# Revit family: UB90.xxx.S
name_source: partatom
category: Möbelsysteme
revit_build: Autodesk Revit 2015 (Build: 20140606_1530(x64)
units: mm (PartAtom-declared; Revit-internal decimal feet)

## types (20) — shared parameters
1400/600 2S 2nd lvl = Nein
Beschreibung = GS-tested safety storage underbench cabinets for unrestricted storage of flammable hazardous materials in work areas in accordance with EN 14470-1 and TRGS 510 with a fire resistance of 90 (Type 90)
Cabinet & door colour = RAL 7035 Light grey
Cabinet height = 600 mm
Diff. pressure (Air change 10 times) = 1.0 Pa
Double door 1400 = Nein
Hersteller = asecos GmbH
Price information = Price from fall 2017
Price information 2 = Prices are ex works and without taxes and shipping
Product video = https://www.youtube.com
Typenbild = <Keine Auswahl>
URL = https://www.asecos.com
ex. air pos. 2 = 130 mm  [stored 0.426509 ft]
zero-valued in all types: Drawer Pos. 1, Drawer Pos. 2

## per-type parameters (varying)
- UB90.060.089.S: 1100/500 2S 2nd lvl=Nein; 1100/500 2S perf. insert=Nein; 1100/500 2nd lvl=Nein; 1100/500 S perf. insert=Nein; 1100/600 2S 2nd lvl=Nein; 1100/600 2S perf. insert=Nein; 1100/600 2nd lvl=Nein; 1100/600 S perf. insert=Nein; 1400/500 2S 2nd lvl=Nein; 1400/500 2S perf. insert=Nein; 1400/600 2S perf. insert=Nein; 590/500 2nd lvl=Nein; 590/500 perf. insert=Nein; 590/600 2nd lvl=Nein; 590/600 perf. insert=Nein; 890/500 2nd lvl=Nein; 890/500 perf. insert=Nein; 890/600 2nd lvl=Nein; 890/600 perf. insert=Ja; Air change 10 times=0.6 L/s; Bestellnummer DACH=30457-001-30459; Cabinet depth=574 mm  [stored 1.8832 ft]; Cabinet width=893 mm  [stored 2.92979 ft]; Distributed load=3.07 kN/m²; Door width=839 mm; Door width RS=495 mm; Double door=Nein; Drawer depth=503 mm  [stored 1.65026 ft]; Drawer width 1=725 mm  [stored 2.37861 ft]; Drawer width 2=100 mm  [stored 0.328084 ft]; Handle LI=Nein; Handle LI pos=178 mm; Handle MI=Ja; Handle MI position=355 mm; Handle RE=Nein; Handle RE Pos=183 mm; Kosten=1693.5 $; Modell=UB90.060.089.S, light grey, drawer with perforated insert; Order No. Global=30457-001-30459; Single door=Ja; Sticker HI=Ja; Sticker LO=Nein; ex. air pos. 1=301 mm  [stored 0.987533 ft]
- UB90.060.059.050.S: 1100/500 2S 2nd lvl=Nein; 1100/500 2S perf. insert=Nein; 1100/500 2nd lvl=Nein; 1100/500 S perf. insert=Nein; 1100/600 2S 2nd lvl=Nein; 1100/600 2S perf. insert=Nein; 1100/600 2nd lvl=Nein; 1100/600 S perf. insert=Nein; 1400/500 2S 2nd lvl=Nein; 1400/500 2S perf. insert=Nein; 1400/600 2S perf. insert=Nein; 590/500 2nd lvl=Nein; 590/500 perf. insert=Ja; 590/600 2nd lvl=Nein; 590/600 perf. insert=Nein; 890/500 2nd lvl=Nein; 890/500 perf. insert=Nein; 890/600 2nd lvl=Nein; 890/600 perf. insert=Nein; Air change 10 times=0.3 L/s; Bestellnummer DACH=30473-001-35294 + 18922; Cabinet depth=503 mm  [stored 1.65026 ft]; Cabinet width=593 mm  [stored 1.94554 ft]; Distributed load=4.51 kN/m²; Door width=539 mm; Door width RS=495 mm; Double door=Nein; Drawer depth=431 mm  [stored 1.41404 ft]; Drawer width 1=425 mm  [stored 1.39436 ft]; Drawer width 2=100 mm  [stored 0.328084 ft]; Handle LI=Nein; Handle LI pos=178 mm; Handle MI=Ja; Handle MI position=205 mm; Handle RE=Nein; Handle RE Pos=183 mm; Kosten=1293 $; Modell=UB90.060.059.050.S, light grey, drawer with perforated insert; Order No. Global=30473-001-35294 + 18922; Single door=Ja; Sticker HI=Nein; Sticker LO=Ja; ex. air pos. 1=182 mm
- UB90.060.059.S: 1100/500 2S 2nd lvl=Nein; 1100/500 2S perf. insert=Nein; 1100/500 2nd lvl=Nein; 1100/500 S perf. insert=Nein; 1100/600 2S 2nd lvl=Nein; 1100/600 2S perf. insert=Nein; 1100/600 2nd lvl=Nein; 1100/600 S perf. insert=Nein; 1400/500 2S 2nd lvl=Nein; 1400/500 2S perf. insert=Nein; 1400/600 2S perf. insert=Nein; 590/500 2nd lvl=Nein; 590/500 perf. insert=Nein; 590/600 2nd lvl=Nein; 590/600 perf. insert=Ja; 890/500 2nd lvl=Nein; 890/500 perf. insert=Nein; 890/600 2nd lvl=Nein; 890/600 perf. insert=Nein; Air change 10 times=0.3 L/s; Bestellnummer DACH=30472-001-30474; Cabinet depth=574 mm  [stored 1.8832 ft]; Cabinet width=593 mm  [stored 1.94554 ft]; Distributed load=4.41 kN/m²; Door width=539 mm; Door width RS=495 mm; Double door=Nein; Drawer depth=503 mm  [stored 1.65026 ft]; Drawer width 1=425 mm  [stored 1.39436 ft]; Drawer width 2=100 mm  [stored 0.328084 ft]; Handle LI=Nein; Handle LI pos=178 mm; Handle MI=Ja; Handle MI position=205 mm; Handle RE=Nein; Handle RE Pos=183 mm; Kosten=1336.5 $; Modell=UB90.060.059.S, light grey, drawer with perforated insert; Order No. Global=30472-001-30474; Single door=Ja; Sticker HI=Nein; Sticker LO=Ja; ex. air pos. 1=182 mm
- UB90.060.110.050.2S: 1100/500 2S 2nd lvl=Nein; 1100/500 2S perf. insert=Ja; 1100/500 2nd lvl=Nein; 1100/500 S perf. insert=Nein; 1100/600 2S 2nd lvl=Nein; 1100/600 2S perf. insert=Nein; 1100/600 2nd lvl=Nein; 1100/600 S perf. insert=Nein; 1400/500 2S 2nd lvl=Nein; 1400/500 2S perf. insert=Nein; 1400/600 2S perf. insert=Nein; 590/500 2nd lvl=Nein; 590/500 perf. insert=Nein; 590/600 2nd lvl=Nein; 590/600 perf. insert=Nein; 890/500 2nd lvl=Nein; 890/500 perf. insert=Nein; 890/600 2nd lvl=Nein; 890/600 perf. insert=Nein; Air change 10 times=0.6 L/s; Bestellnummer DACH=30428-001-35336; Cabinet depth=503 mm  [stored 1.65026 ft]; Cabinet width=1102 mm  [stored 3.61549 ft]; Distributed load=2.73 kN/m²; Door width=521 mm  [stored 1.70932 ft]; Door width RS=521 mm  [stored 1.70932 ft]; Double door=Ja; Drawer depth=431 mm  [stored 1.41404 ft]; Drawer width 1=425 mm  [stored 1.39436 ft]; Drawer width 2=425 mm  [stored 1.39436 ft]; Handle LI=Ja; Handle LI pos=178 mm; Handle MI=Nein; Handle MI position=197 mm; Handle RE=Ja; Handle RE Pos=197 mm; Kosten=2177 $; Modell=UB90.060.110.050.2S, light grey, drawer with perforated insert; Order No. Global=30428-001-35336; Single door=Nein; Sticker HI=Ja; Sticker LO=Nein; ex. air pos. 1=301 mm  [stored 0.987533 ft]
- UB90.060.089.050.S: 1100/500 2S 2nd lvl=Nein; 1100/500 2S perf. insert=Nein; 1100/500 2nd lvl=Nein; 1100/500 S perf. insert=Nein; 1100/600 2S 2nd lvl=Nein; 1100/600 2S perf. insert=Nein; 1100/600 2nd lvl=Nein; 1100/600 S perf. insert=Nein; 1400/500 2S 2nd lvl=Nein; 1400/500 2S perf. insert=Nein; 1400/600 2S perf. insert=Nein; 590/500 2nd lvl=Nein; 590/500 perf. insert=Nein; 590/600 2nd lvl=Nein; 590/600 perf. insert=Nein; 890/500 2nd lvl=Nein; 890/500 perf. insert=Ja; 890/600 2nd lvl=Nein; 890/600 perf. insert=Nein; Air change 10 times=0.3 L/s; Bestellnummer DACH=30458-001-35307; Cabinet depth=503 mm  [stored 1.65026 ft]; Cabinet width=893 mm  [stored 2.92979 ft]; Distributed load=3.11 kN/m²; Door width=839 mm; Door width RS=495 mm; Double door=Nein; Drawer depth=431 mm  [stored 1.41404 ft]; Drawer width 1=725 mm  [stored 2.37861 ft]; Drawer width 2=100 mm  [stored 0.328084 ft]; Handle LI=Nein; Handle LI pos=178 mm; Handle MI=Ja; Handle MI position=355 mm; Handle RE=Nein; Handle RE Pos=183 mm; Kosten=1630 $; Modell=UB90.060.089.050.S, light grey, drawer with perforated insert; Order No. Global=30458-001-35307; Single door=Ja; Sticker HI=Ja; Sticker LO=Nein; ex. air pos. 1=301 mm  [stored 0.987533 ft]
- UB90.060.110.2S: 1100/500 2S 2nd lvl=Nein; 1100/500 2S perf. insert=Nein; 1100/500 2nd lvl=Nein; 1100/500 S perf. insert=Nein; 1100/600 2S 2nd lvl=Nein; 1100/600 2S perf. insert=Ja; 1100/600 2nd lvl=Nein; 1100/600 S perf. insert=Nein; 1400/500 2S 2nd lvl=Nein; 1400/500 2S perf. insert=Nein; 1400/600 2S perf. insert=Nein; 590/500 2nd lvl=Nein; 590/500 perf. insert=Nein; 590/600 2nd lvl=Nein; 590/600 perf. insert=Nein; 890/500 2nd lvl=Nein; 890/500 perf. insert=Nein; 890/600 2nd lvl=Nein; 890/600 perf. insert=Nein; Air change 10 times=0.6 L/s; Bestellnummer DACH=30427-001-30430; Cabinet depth=574 mm  [stored 1.8832 ft]; Cabinet width=1102 mm  [stored 3.61549 ft]; Distributed load=2.72 kN/m²; Door width=521 mm  [stored 1.70932 ft]; Door width RS=521 mm  [stored 1.70932 ft]; Double door=Ja; Drawer depth=503 mm  [stored 1.65026 ft]; Drawer width 1=425 mm  [stored 1.39436 ft]; Drawer width 2=425 mm  [stored 1.39436 ft]; Handle LI=Ja; Handle LI pos=175 mm  [stored 0.574147 ft]; Handle MI=Nein; Handle MI position=197 mm; Handle RE=Ja; Handle RE Pos=47 mm  [stored 0.154199 ft]; Kosten=2264 $; Modell=UB90.060.110.2S, light grey, drawer with perforated insert; Order No. Global=30427-001-30430; Single door=Nein; Sticker HI=Ja; Sticker LO=Nein; ex. air pos. 1=301 mm  [stored 0.987533 ft]
- UB90.060.140.2S: 1100/500 2S 2nd lvl=Nein; 1100/500 2S perf. insert=Nein; 1100/500 2nd lvl=Nein; 1100/500 S perf. insert=Nein; 1100/600 2S 2nd lvl=Nein; 1100/600 2S perf. insert=Nein; 1100/600 2nd lvl=Nein; 1100/600 S perf. insert=Nein; 1400/500 2S 2nd lvl=Nein; 1400/500 2S perf. insert=Nein; 1400/600 2S perf. insert=Ja; 590/500 2nd lvl=Nein; 590/500 perf. insert=Nein; 590/600 2nd lvl=Nein; 590/600 perf. insert=Nein; 890/500 2nd lvl=Nein; 890/500 perf. insert=Nein; 890/600 2nd lvl=Nein; 890/600 perf. insert=Nein; Air change 10 times=0.8 L/s; Bestellnummer DACH=30401-001-30404; Cabinet depth=574 mm  [stored 1.8832 ft]; Cabinet width=1402 mm  [stored 4.59974 ft]; Distributed load=2.35 kN/m²; Door width=821 mm  [stored 2.69357 ft]; Door width RS=521 mm  [stored 1.70932 ft]; Double door=Ja; Drawer depth=503 mm  [stored 1.65026 ft]; Drawer width 1=725 mm  [stored 2.37861 ft]; Drawer width 2=425 mm  [stored 1.39436 ft]; Handle LI=Nein; Handle LI pos=175 mm  [stored 0.574147 ft]; Handle MI=Ja; Handle MI position=347 mm; Handle RE=Ja; Handle RE Pos=47 mm  [stored 0.154199 ft]; Kosten=2370 $; Modell=UB90.060.140.2S, light grey, drawer with perforated insert; Order No. Global=30401-001-30404; Single door=Nein; Sticker HI=Ja; Sticker LO=Nein; ex. air pos. 1=301 mm  [stored 0.987533 ft]
- UB90.060.110.S: 1100/500 2S 2nd lvl=Nein; 1100/500 2S perf. insert=Nein; 1100/500 2nd lvl=Nein; 1100/500 S perf. insert=Nein; 1100/600 2S 2nd lvl=Nein; 1100/600 2S perf. insert=Nein; 1100/600 2nd lvl=Nein; 1100/600 S perf. insert=Ja; 1400/500 2S 2nd lvl=Nein; 1400/500 2S perf. insert=Nein; 1400/600 2S perf. insert=Nein; 590/500 2nd lvl=Nein; 590/500 perf. insert=Nein; 590/600 2nd lvl=Nein; 590/600 perf. insert=Nein; 890/500 2nd lvl=Nein; 890/500 perf. insert=Nein; 890/600 2nd lvl=Nein; 890/600 perf. insert=Nein; Air change 10 times=0.6 L/s; Bestellnummer DACH=30420-001-30423; Cabinet depth=574 mm  [stored 1.8832 ft]; Cabinet width=1102 mm  [stored 3.61549 ft]; Distributed load=2.72 kN/m²; Door width=1048 mm; Door width RS=495 mm; Double door=Nein; Drawer depth=503 mm  [stored 1.65026 ft]; Drawer width 1=934 mm  [stored 3.0643 ft]; Drawer width 2=100 mm  [stored 0.328084 ft]; Handle LI=Nein; Handle LI pos=178 mm; Handle MI=Ja; Handle MI position=460 mm; Handle RE=Nein; Handle RE Pos=183 mm; Kosten=1761 $; Modell=UB90.060.110.S, light grey, drawer with perforated insert; Order No. Global=30420-001-30423; Single door=Ja; Sticker HI=Ja; Sticker LO=Nein; ex. air pos. 1=301 mm  [stored 0.987533 ft]
- UB90.060.110.050.S: 1100/500 2S 2nd lvl=Nein; 1100/500 2S perf. insert=Nein; 1100/500 2nd lvl=Nein; 1100/500 S perf. insert=Ja; 1100/600 2S 2nd lvl=Nein; 1100/600 2S perf. insert=Nein; 1100/600 2nd lvl=Nein; 1100/600 S perf. insert=Nein; 1400/500 2S 2nd lvl=Nein; 1400/500 2S perf. insert=Nein; 1400/600 2S perf. insert=Nein; 590/500 2nd lvl=Nein; 590/500 perf. insert=Nein; 590/600 2nd lvl=Nein; 590/600 perf. insert=Nein; 890/500 2nd lvl=Nein; 890/500 perf. insert=Nein; 890/600 2nd lvl=Nein; 890/600 perf. insert=Nein; Air change 10 times=0.6 L/s; Bestellnummer DACH=30421-001-35339; Cabinet depth=503 mm  [stored 1.65026 ft]; Cabinet width=1102 mm  [stored 3.61549 ft]; Distributed load=2.73 kN/m²; Door width=1048 mm; Door width RS=495 mm; Double door=Nein; Drawer depth=431 mm  [stored 1.41404 ft]; Drawer width 1=934 mm  [stored 3.0643 ft]; Drawer width 2=100 mm  [stored 0.328084 ft]; Handle LI=Nein; Handle LI pos=178 mm; Handle MI=Ja; Handle MI position=460 mm; Handle RE=Nein; Handle RE Pos=183 mm; Kosten=1682 $; Modell=UB90.060.110.050.S, light grey, drawer with perforated insert; Order No. Global=30421-001-35339; Single door=Ja; Sticker HI=Ja; Sticker LO=Nein; ex. air pos. 1=301 mm  [stored 0.987533 ft]
- UB90.060.140.050.2S: 1100/500 2S 2nd lvl=Nein; 1100/500 2S perf. insert=Nein; 1100/500 2nd lvl=Nein; 1100/500 S perf. insert=Nein; 1100/600 2S 2nd lvl=Nein; 1100/600 2S perf. insert=Nein; 1100/600 2nd lvl=Nein; 1100/600 S perf. insert=Nein; 1400/500 2S 2nd lvl=Nein; 1400/500 2S perf. insert=Ja; 1400/600 2S perf. insert=Nein; 590/500 2nd lvl=Nein; 590/500 perf. insert=Nein; 590/600 2nd lvl=Nein; 590/600 perf. insert=Nein; 890/500 2nd lvl=Nein; 890/500 perf. insert=Nein; 890/600 2nd lvl=Nein; 890/600 perf. insert=Nein; Air change 10 times=0.8 L/s; Bestellnummer DACH=30402-001-35358 + 18922; Cabinet depth=503 mm  [stored 1.65026 ft]; Cabinet width=1402 mm  [stored 4.59974 ft]; Distributed load=2.35 kN/m²; Door width=821 mm  [stored 2.69357 ft]; Door width RS=521 mm  [stored 1.70932 ft]; Double door=Ja; Drawer depth=431 mm  [stored 1.41404 ft]; Drawer width 1=725 mm  [stored 2.37861 ft]; Drawer width 2=425 mm  [stored 1.39436 ft]; Handle LI=Nein; Handle LI pos=175 mm  [stored 0.574147 ft]; Handle MI=Ja; Handle MI position=347 mm; Handle RE=Ja; Handle RE Pos=47 mm  [stored 0.154199 ft]; Kosten=2263 $; Modell=UB90.060.140.050.2S, light grey, drawer with perforated insert; Order No. Global=30402-001-35358 + 18922; Single door=Nein; Sticker HI=Ja; Sticker LO=Nein; ex. air pos. 1=301 mm  [stored 0.987533 ft]
- UB90.060.059.050.S with second level drawer: 1100/500 2S 2nd lvl=Nein; 1100/500 2S perf. insert=Nein; 1100/500 2nd lvl=Nein; 1100/500 S perf. insert=Nein; 1100/600 2S 2nd lvl=Nein; 1100/600 2S perf. insert=Nein; 1100/600 2nd lvl=Nein; 1100/600 S perf. insert=Nein; 1400/500 2S 2nd lvl=Nein; 1400/500 2S perf. insert=Nein; 1400/600 2S perf. insert=Nein; 590/500 2nd lvl=Ja; 590/500 perf. insert=Ja; 590/600 2nd lvl=Nein; 590/600 perf. insert=Nein; 890/500 2nd lvl=Nein; 890/500 perf. insert=Nein; 890/600 2nd lvl=Nein; 890/600 perf. insert=Nein; Air change 10 times=0.3 L/s; Bestellnummer DACH=30473-001-35294 + 18922 + 16595; Cabinet depth=503 mm  [stored 1.65026 ft]; Cabinet width=593 mm  [stored 1.94554 ft]; Distributed load=4.51 kN/m²; Door width=539 mm; Door width RS=495 mm; Double door=Nein; Drawer depth=431 mm  [stored 1.41404 ft]; Drawer width 1=425 mm  [stored 1.39436 ft]; Drawer width 2=100 mm  [stored 0.328084 ft]; Handle LI=Nein; Handle LI pos=178 mm; Handle MI=Ja; Handle MI position=205 mm; Handle RE=Nein; Handle RE Pos=183 mm; Kosten=1452 $; Modell=UB90.060.059.050.S, light grey, drawer with perforated insert, second level drawer; Order No. Global=30473-001-35294 + 18922 + 16595; Single door=Ja; Sticker HI=Nein; Sticker LO=Ja; ex. air pos. 1=182 mm
- UB90.060.059.S with second level drawer: 1100/500 2S 2nd lvl=Nein; 1100/500 2S perf. insert=Nein; 1100/500 2nd lvl=Nein; 1100/500 S perf. insert=Nein; 1100/600 2S 2nd lvl=Nein; 1100/600 2S perf. insert=Nein; 1100/600 2nd lvl=Nein; 1100/600 S perf. insert=Nein; 1400/500 2S 2nd lvl=Nein; 1400/500 2S perf. insert=Nein; 1400/600 2S perf. insert=Nein; 590/500 2nd lvl=Nein; 590/500 perf. insert=Nein; 590/600 2nd lvl=Ja; 590/600 perf. insert=Ja; 890/500 2nd lvl=Nein; 890/500 perf. insert=Nein; 890/600 2nd lvl=Nein; 890/600 perf. insert=Nein; Air change 10 times=0.3 L/s; Bestellnummer DACH=30472-001-30475; Cabinet depth=574 mm  [stored 1.8832 ft]; Cabinet width=593 mm  [stored 1.94554 ft]; Distributed load=4.41 kN/m²; Door width=539 mm; Door width RS=495 mm; Double door=Nein; Drawer depth=503 mm  [stored 1.65026 ft]; Drawer width 1=425 mm  [stored 1.39436 ft]; Drawer width 2=100 mm  [stored 0.328084 ft]; Handle LI=Nein; Handle LI pos=178 mm; Handle MI=Ja; Handle MI position=205 mm; Handle RE=Nein; Handle RE Pos=183 mm; Kosten=1465.5 $; Modell=UB90.060.059.S, light grey, drawer with perforated insert, second level drawer; Order No. Global=30472-001-30475; Single door=Ja; Sticker HI=Nein; Sticker LO=Ja; ex. air pos. 1=182 mm
- UB90.060.089.050.S with second level drawer: 1100/500 2S 2nd lvl=Nein; 1100/500 2S perf. insert=Nein; 1100/500 2nd lvl=Nein; 1100/500 S perf. insert=Nein; 1100/600 2S 2nd lvl=Nein; 1100/600 2S perf. insert=Nein; 1100/600 2nd lvl=Nein; 1100/600 S perf. insert=Nein; 1400/500 2S 2nd lvl=Nein; 1400/500 2S perf. insert=Nein; 1400/600 2S perf. insert=Nein; 590/500 2nd lvl=Nein; 590/500 perf. insert=Nein; 590/600 2nd lvl=Nein; 590/600 perf. insert=Nein; 890/500 2nd lvl=Ja; 890/500 perf. insert=Ja; 890/600 2nd lvl=Nein; 890/600 perf. insert=Nein; Air change 10 times=0.3 L/s; Bestellnummer DACH=30458-001-35307 + 16589; Cabinet depth=503 mm  [stored 1.65026 ft]; Cabinet width=893 mm  [stored 2.92979 ft]; Distributed load=3.11 kN/m²; Door width=839 mm; Door width RS=495 mm; Double door=Nein; Drawer depth=431 mm  [stored 1.41404 ft]; Drawer width 1=725 mm  [stored 2.37861 ft]; Drawer width 2=100 mm  [stored 0.328084 ft]; Handle LI=Nein; Handle LI pos=178 mm; Handle MI=Ja; Handle MI position=355 mm; Handle RE=Nein; Handle RE Pos=183 mm; Kosten=1803 $; Modell=UB90.060.089.050.S, light grey, drawer with perforated insert, second level drawer; Order No. Global=30458-001-35307 + 16589; Single door=Ja; Sticker HI=Ja; Sticker LO=Nein; ex. air pos. 1=301 mm  [stored 0.987533 ft]
- UB90.060.089.S with second level drawer: 1100/500 2S 2nd lvl=Nein; 1100/500 2S perf. insert=Nein; 1100/500 2nd lvl=Nein; 1100/500 S perf. insert=Nein; 1100/600 2S 2nd lvl=Nein; 1100/600 2S perf. insert=Nein; 1100/600 2nd lvl=Nein; 1100/600 S perf. insert=Nein; 1400/500 2S 2nd lvl=Nein; 1400/500 2S perf. insert=Nein; 1400/600 2S perf. insert=Nein; 590/500 2nd lvl=Nein; 590/500 perf. insert=Nein; 590/600 2nd lvl=Nein; 590/600 perf. insert=Nein; 890/500 2nd lvl=Nein; 890/500 perf. insert=Nein; 890/600 2nd lvl=Ja; 890/600 perf. insert=Ja; Air change 10 times=0.6 L/s; Bestellnummer DACH=30457-001-30460; Cabinet depth=574 mm  [stored 1.8832 ft]; Cabinet width=893 mm  [stored 2.92979 ft]; Distributed load=3.07 kN/m²; Door width=839 mm; Door width RS=495 mm; Double door=Nein; Drawer depth=503 mm  [stored 1.65026 ft]; Drawer width 1=725 mm  [stored 2.37861 ft]; Drawer width 2=100 mm  [stored 0.328084 ft]; Handle LI=Nein; Handle LI pos=178 mm; Handle MI=Ja; Handle MI position=355 mm; Handle RE=Nein; Handle RE Pos=183 mm; Kosten=1830.5 $; Modell=UB90.060.089.S, light grey, drawer with perforated insert, second level drawer; Order No. Global=30457-001-30460; Single door=Ja; Sticker HI=Ja; Sticker LO=Nein; ex. air pos. 1=301 mm  [stored 0.987533 ft]
- UB90.060.110.050.2S with second level drawer: 1100/500 2S 2nd lvl=Ja; 1100/500 2S perf. insert=Ja; 1100/500 2nd lvl=Nein; 1100/500 S perf. insert=Nein; 1100/600 2S 2nd lvl=Nein; 1100/600 2S perf. insert=Nein; 1100/600 2nd lvl=Nein; 1100/600 S perf. insert=Nein; 1400/500 2S 2nd lvl=Nein; 1400/500 2S perf. insert=Nein; 1400/600 2S perf. insert=Nein; 590/500 2nd lvl=Nein; 590/500 perf. insert=Nein; 590/600 2nd lvl=Nein; 590/600 perf. insert=Nein; 890/500 2nd lvl=Nein; 890/500 perf. insert=Nein; 890/600 2nd lvl=Nein; 890/600 perf. insert=Nein; Air change 10 times=0.6 L/s; Bestellnummer DACH=30428-001-35336 + 16590; Cabinet depth=503 mm  [stored 1.65026 ft]; Cabinet width=1102 mm  [stored 3.61549 ft]; Distributed load=2.73 kN/m²; Door width=521 mm  [stored 1.70932 ft]; Door width RS=521 mm  [stored 1.70932 ft]; Double door=Ja; Drawer depth=431 mm  [stored 1.41404 ft]; Drawer width 1=425 mm  [stored 1.39436 ft]; Drawer width 2=425 mm  [stored 1.39436 ft]; Handle LI=Ja; Handle LI pos=178 mm; Handle MI=Nein; Handle MI position=197 mm; Handle RE=Ja; Handle RE Pos=197 mm; Kosten=2347 $; Modell=UB90.060.110.050.2S, light grey, drawer with perforated insert,second level drawer; Order No. Global=30428-001-35336 + 16590; Single door=Nein; Sticker HI=Ja; Sticker LO=Nein; ex. air pos. 1=301 mm  [stored 0.987533 ft]
- UB90.060.110.050.S with second level drawer: 1100/500 2S 2nd lvl=Nein; 1100/500 2S perf. insert=Nein; 1100/500 2nd lvl=Ja; 1100/500 S perf. insert=Ja; 1100/600 2S 2nd lvl=Nein; 1100/600 2S perf. insert=Nein; 1100/600 2nd lvl=Nein; 1100/600 S perf. insert=Nein; 1400/500 2S 2nd lvl=Nein; 1400/500 2S perf. insert=Nein; 1400/600 2S perf. insert=Nein; 590/500 2nd lvl=Nein; 590/500 perf. insert=Nein; 590/600 2nd lvl=Nein; 590/600 perf. insert=Nein; 890/500 2nd lvl=Nein; 890/500 perf. insert=Nein; 890/600 2nd lvl=Nein; 890/600 perf. insert=Nein; Air change 10 times=0.6 L/s; Bestellnummer DACH=30421-001-35339 + 16592; Cabinet depth=503 mm  [stored 1.65026 ft]; Cabinet width=1102 mm  [stored 3.61549 ft]; Distributed load=2.73 kN/m²; Door width=1048 mm; Door width RS=495 mm; Double door=Nein; Drawer depth=431 mm  [stored 1.41404 ft]; Drawer width 1=934 mm  [stored 3.0643 ft]; Drawer width 2=100 mm  [stored 0.328084 ft]; Handle LI=Nein; Handle LI pos=178 mm; Handle MI=Ja; Handle MI position=460 mm; Handle RE=Nein; Handle RE Pos=183 mm; Kosten=1861 $; Modell=UB90.060.110.050.S, light grey, drawer with perforated insert, second level drawer; Order No. Global=30421-001-35339 + 16592; Single door=Ja; Sticker HI=Ja; Sticker LO=Nein; ex. air pos. 1=301 mm  [stored 0.987533 ft]
- UB90.060.110.2S with second level drawer: 1100/500 2S 2nd lvl=Nein; 1100/500 2S perf. insert=Nein; 1100/500 2nd lvl=Nein; 1100/500 S perf. insert=Nein; 1100/600 2S 2nd lvl=Ja; 1100/600 2S perf. insert=Ja; 1100/600 2nd lvl=Nein; 1100/600 S perf. insert=Nein; 1400/500 2S 2nd lvl=Nein; 1400/500 2S perf. insert=Nein; 1400/600 2S perf. insert=Nein; 590/500 2nd lvl=Nein; 590/500 perf. insert=Nein; 590/600 2nd lvl=Nein; 590/600 perf. insert=Nein; 890/500 2nd lvl=Nein; 890/500 perf. insert=Nein; 890/600 2nd lvl=Nein; 890/600 perf. insert=Nein; Air change 10 times=0.6 L/s; Bestellnummer DACH=30427-001-30431; Cabinet depth=574 mm  [stored 1.8832 ft]; Cabinet width=1102 mm  [stored 3.61549 ft]; Distributed load=2.72 kN/m²; Door width=521 mm  [stored 1.70932 ft]; Door width RS=521 mm  [stored 1.70932 ft]; Double door=Ja; Drawer depth=503 mm  [stored 1.65026 ft]; Drawer width 1=425 mm  [stored 1.39436 ft]; Drawer width 2=425 mm  [stored 1.39436 ft]; Handle LI=Ja; Handle LI pos=175 mm  [stored 0.574147 ft]; Handle MI=Nein; Handle MI position=197 mm; Handle RE=Ja; Handle RE Pos=47 mm  [stored 0.154199 ft]; Kosten=2522 $; Modell=UB90.060.110.2S, light grey, drawer with perforated insert, second level drawer; Order No. Global=30427-001-30431; Single door=Nein; Sticker HI=Ja; Sticker LO=Nein; ex. air pos. 1=301 mm  [stored 0.987533 ft]
- UB90.060.110.S with second level drawer: 1100/500 2S 2nd lvl=Nein; 1100/500 2S perf. insert=Nein; 1100/500 2nd lvl=Nein; 1100/500 S perf. insert=Nein; 1100/600 2S 2nd lvl=Nein; 1100/600 2S perf. insert=Nein; 1100/600 2nd lvl=Ja; 1100/600 S perf. insert=Ja; 1400/500 2S 2nd lvl=Nein; 1400/500 2S perf. insert=Nein; 1400/600 2S perf. insert=Nein; 590/500 2nd lvl=Nein; 590/500 perf. insert=Nein; 590/600 2nd lvl=Nein; 590/600 perf. insert=Nein; 890/500 2nd lvl=Nein; 890/500 perf. insert=Nein; 890/600 2nd lvl=Nein; 890/600 perf. insert=Nein; Air change 10 times=0.6 L/s; Bestellnummer DACH=30420-001-30424; Cabinet depth=574 mm  [stored 1.8832 ft]; Cabinet width=1102 mm  [stored 3.61549 ft]; Distributed load=2.72 kN/m²; Door width=1048 mm; Door width RS=495 mm; Double door=Nein; Drawer depth=503 mm  [stored 1.65026 ft]; Drawer width 1=934 mm  [stored 3.0643 ft]; Drawer width 2=100 mm  [stored 0.328084 ft]; Handle LI=Nein; Handle LI pos=178 mm; Handle MI=Ja; Handle MI position=460 mm; Handle RE=Nein; Handle RE Pos=183 mm; Kosten=1898 $; Modell=UB90.060.110.050.2S, light grey, drawer with perforated insert, second level drawer; Order No. Global=30420-001-30424; Single door=Ja; Sticker HI=Ja; Sticker LO=Nein; ex. air pos. 1=301 mm  [stored 0.987533 ft]
- UB90.060.140.050.2S with second level drawer: 1100/500 2S 2nd lvl=Nein; 1100/500 2S perf. insert=Nein; 1100/500 2nd lvl=Nein; 1100/500 S perf. insert=Nein; 1100/600 2S 2nd lvl=Nein; 1100/600 2S perf. insert=Nein; 1100/600 2nd lvl=Nein; 1100/600 S perf. insert=Nein; 1400/500 2S 2nd lvl=Ja; 1400/500 2S perf. insert=Ja; 1400/600 2S perf. insert=Nein; 590/500 2nd lvl=Nein; 590/500 perf. insert=Nein; 590/600 2nd lvl=Nein; 590/600 perf. insert=Nein; 890/500 2nd lvl=Nein; 890/500 perf. insert=Nein; 890/600 2nd lvl=Nein; 890/600 perf. insert=Nein; Air change 10 times=0.8 L/s; Bestellnummer DACH=30402-001-35358 + 18922 + 16590 +16589; Cabinet depth=503 mm  [stored 1.65026 ft]; Cabinet width=1402 mm  [stored 4.59974 ft]; Distributed load=2.35 kN/m²; Door width=821 mm  [stored 2.69357 ft]; Door width RS=521 mm  [stored 1.70932 ft]; Double door=Ja; Drawer depth=431 mm  [stored 1.41404 ft]; Drawer width 1=725 mm  [stored 2.37861 ft]; Drawer width 2=425 mm  [stored 1.39436 ft]; Handle LI=Nein; Handle LI pos=175 mm  [stored 0.574147 ft]; Handle MI=Ja; Handle MI position=347 mm; Handle RE=Ja; Handle RE Pos=47 mm  [stored 0.154199 ft]; Kosten=2606 $; Modell=UB90.060.140.050.2S, light grey, drawer with perforated insert, second level drawer; Order No. Global=30402-001-35358 + 18922 + 16590 +16589; Single door=Nein; Sticker HI=Ja; Sticker LO=Nein; ex. air pos. 1=301 mm  [stored 0.987533 ft]
- UB90.060.140.2S with second level drawer: 1100/500 2S 2nd lvl=Nein; 1100/500 2S perf. insert=Nein; 1100/500 2nd lvl=Nein; 1100/500 S perf. insert=Nein; 1100/600 2S 2nd lvl=Nein; 1100/600 2S perf. insert=Nein; 1100/600 2nd lvl=Nein; 1100/600 S perf. insert=Nein; 1400/500 2S 2nd lvl=Ja; 1400/500 2S perf. insert=Nein; 1400/600 2S perf. insert=Ja; 590/500 2nd lvl=Nein; 590/500 perf. insert=Nein; 590/600 2nd lvl=Nein; 590/600 perf. insert=Nein; 890/500 2nd lvl=Nein; 890/500 perf. insert=Nein; 890/600 2nd lvl=Nein; 890/600 perf. insert=Nein; Air change 10 times=0.8 L/s; Bestellnummer DACH=30401-001-30405; Cabinet depth=574 mm  [stored 1.8832 ft]; Cabinet width=1402 mm  [stored 4.59974 ft]; Distributed load=2.35 kN/m²; Door width=821 mm  [stored 2.69357 ft]; Door width RS=521 mm  [stored 1.70932 ft]; Double door=Ja; Drawer depth=503 mm  [stored 1.65026 ft]; Drawer width 1=725 mm  [stored 2.37861 ft]; Drawer width 2=425 mm  [stored 1.39436 ft]; Handle LI=Nein; Handle LI pos=175 mm  [stored 0.574147 ft]; Handle MI=Ja; Handle MI position=347 mm; Handle RE=Ja; Handle RE Pos=47 mm  [stored 0.154199 ft]; Kosten=2636 $; Modell=UB90.060.140.2S, light grey, drawer with perforated insert, second level drawer; Order No. Global=30401-001-30405; Single door=Nein; Sticker HI=Ja; Sticker LO=Nein; ex. air pos. 1=301 mm  [stored 0.987533 ft]

note: [stored X ft] marks values corroborated as IEEE doubles in the binary element streams (Revit-internal decimal feet)
